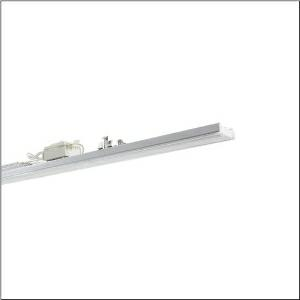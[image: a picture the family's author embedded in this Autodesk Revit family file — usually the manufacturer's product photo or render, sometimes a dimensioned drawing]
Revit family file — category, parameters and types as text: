
# Revit family: licross_r__11_recessed_mo_51tl14de445g_5125
name_source: partatom
category: Lighting Fixtures
units: mm (PartAtom-declared; Revit-internal decimal feet)

## family parameters
Cut with Voids When Loaded = No
Host = Face
Light Source = No
Part Type = Normal
Room Calculation Point = No
Round Connector Dimension = Use Diameter
Shared = No

## types (1)
- --- (1 x LED, 4710 lm, 29.6 W, 4000K)
    Apparent Load = 30 VA
    CIE Flux Codes = 56 84 97 100 100
    Color Rendering = 80
    Color Temperature = 4000K
    Default Elevation = 1800 mm
    Description = Licross® 11 Recessed MO, luminaire insert, of sheet steel, coil coated, white, length: 750mm, width: 66mm, height: 67mm, LED rated luminous flux: 4.710lm, light colour: 840, control gear: DALI 2, with plug, 5-pole, with phase selection, mains connection: 220..240V, AC, 50/60Hz, rated input power: 30W, halogen-free wiring, primary light control with lens, of plastic, primary optical cover: cover, of PMMA, light emission: direct distribution, primary light characteristic: asymmetric, protection rating (complete): IP40, insulation class (complete): insulation class I (protective earthing), certification: CE, ENEC, VDE, UKCA, protection symbol: D if used in an environment without relevant dust loads with corresponding accessories, impact resistance: IK06, permissible ambient temperature for indoor applications: -25..+35°C, corresponds to IFS (International Featured Standards) requirements for safety and quality in the food industry, reducing of maximum allowable ambient temperature of 5°C with ceiling mounting, LABS conformity tested according to VDMA 24364:2018-05, packaging unit: 1 piece
    Height = 58 mm
    Lamp = 1 x LED
    Lamp Light Flux = 4710 lm
    Lamp Power = 29.6 W
    Lamp count = 1
    Length = 750 mm
    Luminous efficacy = 159 lm/W
    Manufacturer = Siteco
    ModVariant = No
    Model = 51TL14DE445G
    Mounting Place = Ceiling
    Mounting Type = Pendant
    Number of Poles = 1
    OnlyDefault = Yes
    Power Factor = 1
    Product Name = Licross® 11 Recessed MO
    Product group = luminaire insert
    ProductGroupID = 902
    Protection Class = Protection class I
    Protection Degree = IP 40
    RLX_Detail_Level = 1
    RLX_Emergency_Light_Flux = 0 lm
    RLX_Emergency_Type = 0
    RLX_Emergency_Type_DB = No
    RlxData = <blob elided: 29437 chars, md5=aef4311a>
    Socket = socket
    Standby Power = 0 W
    System Light Flux = 4710 lm
    System Power = 30 W
    Type Comments = factory setting: luminous flux: 100 % | dim-lin: 254 | 378 mA
    Type Image = l_1296930.jpg
    URL = http://relux.com
    VarID = @adj_099942
    Voltage = 0 V
    Weight = 0.00 kg
    Width = 66 mm

## geometry (parser evidence)
native form markers: Blend x4, Sweep x8
no freeform markers — native parametric forms only
